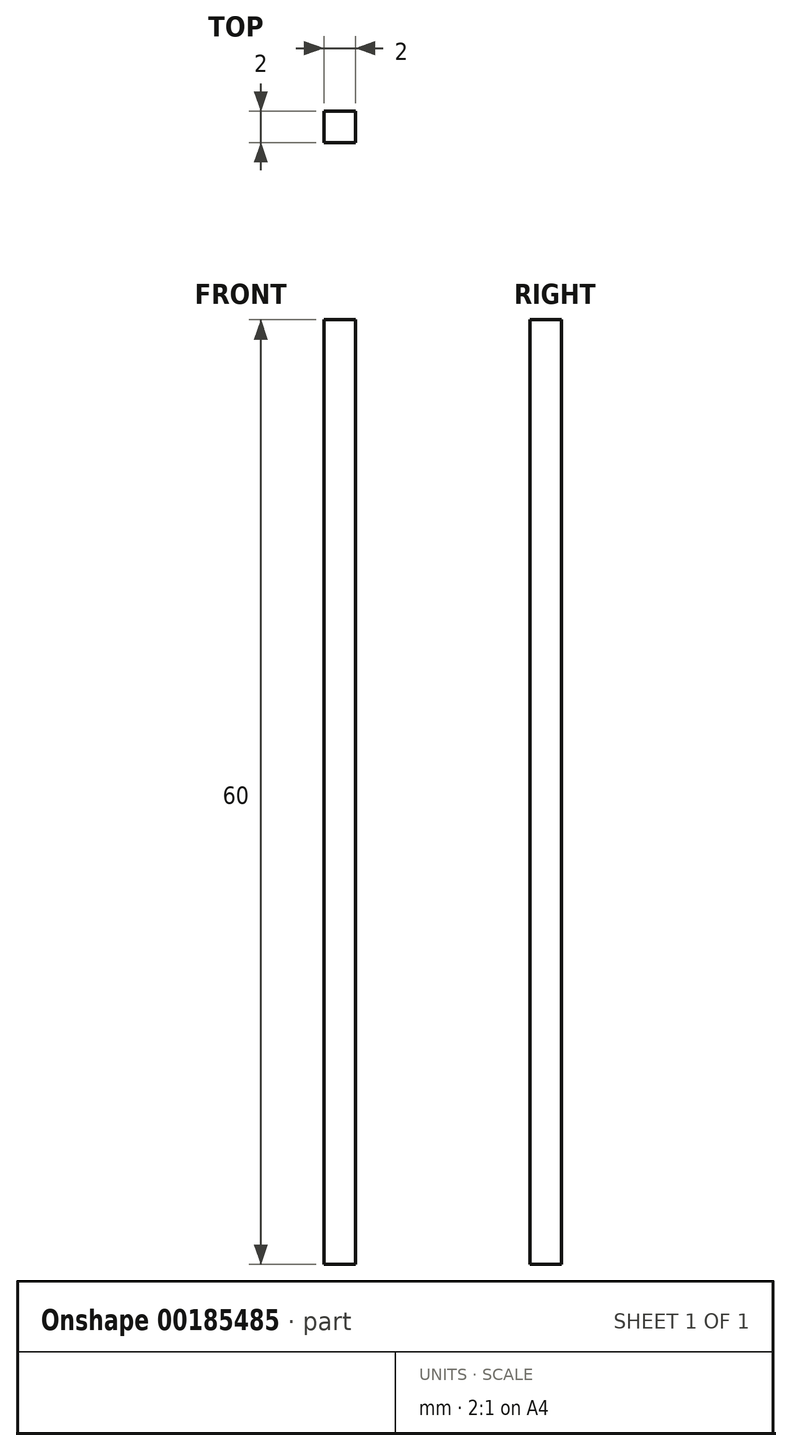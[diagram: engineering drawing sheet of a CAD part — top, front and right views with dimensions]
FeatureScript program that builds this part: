
annotation { "Feature Type Name" : "Feature", "Feature Type Description" : "" }
export const myFeature = defineFeature(function(context is Context, id is Id, definition is map)
    precondition{}
    {
        {
            var Q0;
            Q0=qCreatedBy(makeId("Top.planeOp"),FACE);
            var sketch = newSketch(context, id + "F0", { "sketchPlane" : qUnion([Q0])});
            skLineSegment(sketch, "E0.bottom", {"start": v(0, 0) * mm, "end": v(-2, 0) * mm});
            skLineSegment(sketch, "E0.top", {"start": v(0, 2) * mm, "end": v(-2, 2) * mm});
            skLineSegment(sketch, "E0.left", {"start": v(0, 0) * mm, "end": v(0, 2) * mm});
            skLineSegment(sketch, "E0.right", {"start": v(-2, 0) * mm, "end": v(-2, 2) * mm});
            skSolve(sketch);
        }
        {
            var Q0;
            Q0=qSketchRegion(id+"F0",true);
            extrude(context, id + "F1", {"entities" : qUnion([Q0]), "depth" : 60 * mm});
        }
    });
